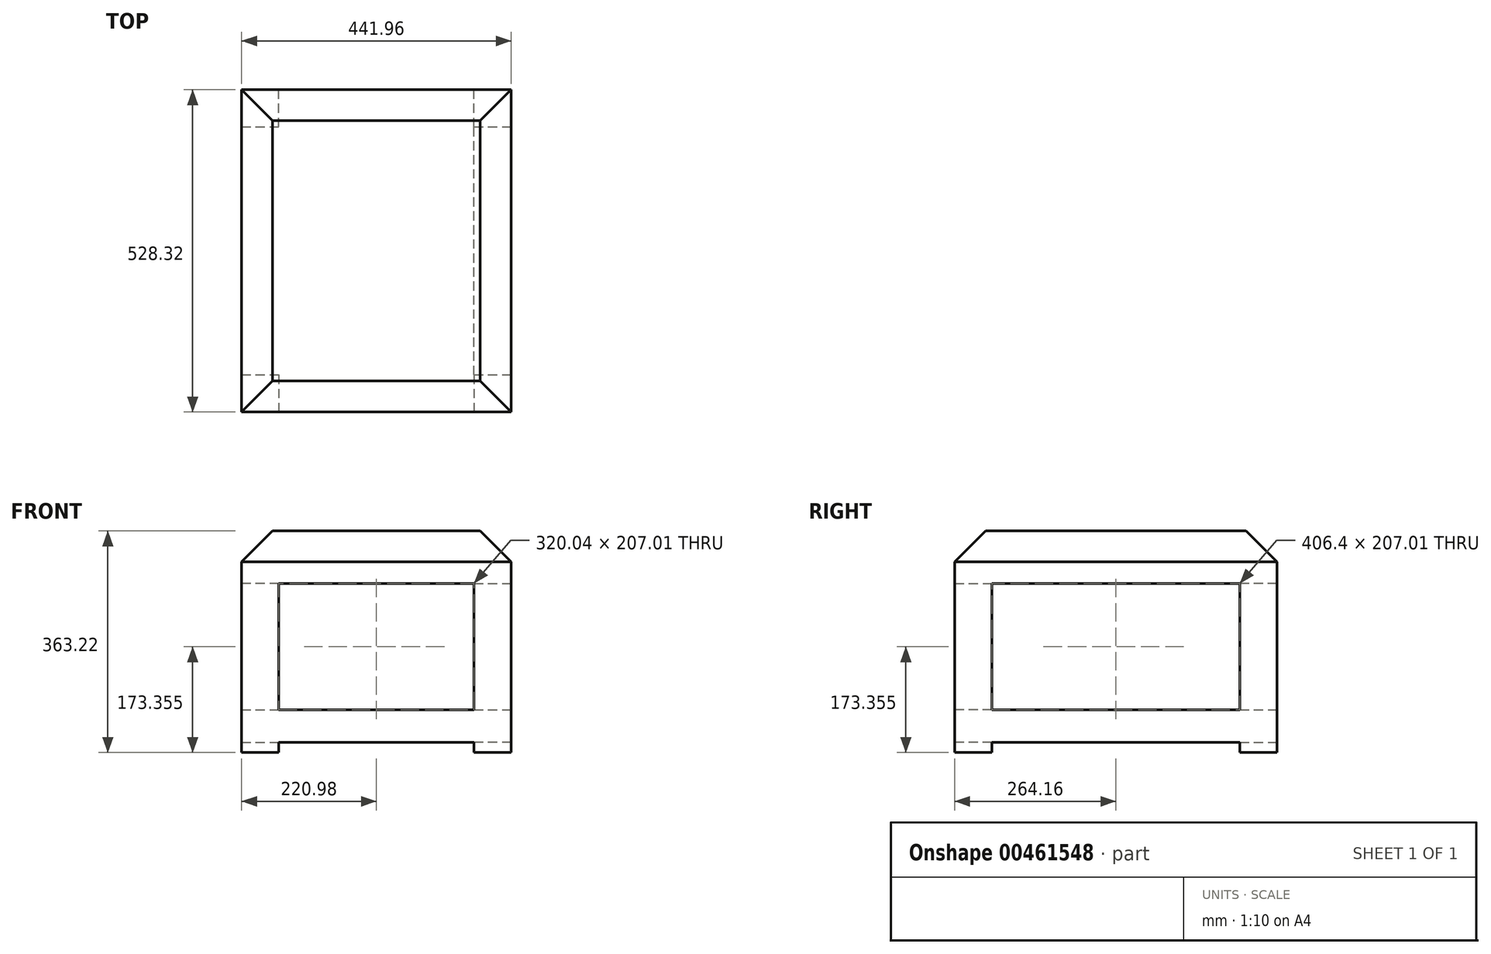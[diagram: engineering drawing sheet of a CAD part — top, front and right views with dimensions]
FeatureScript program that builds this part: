
annotation { "Feature Type Name" : "Feature", "Feature Type Description" : "" }
export const myFeature = defineFeature(function(context is Context, id is Id, definition is map)
    precondition{}
    {
        {
            var Q0;
            Q0=qCreatedBy(makeId("Top.planeOp"),FACE);
            var sketch = newSketch(context, id + "F0", { "sketchPlane" : qUnion([Q0])});
            skLineSegment(sketch, "E0", {"start": v(0, 0) * mm, "end": v(0, -264.16) * mm});
            skLineSegment(sketch, "E1", {"start": v(0, -264.16) * mm, "end": v(220.98, -264.16) * mm});
            skLineSegment(sketch, "E2", {"start": v(220.98, -264.16) * mm, "end": v(220.98, 0) * mm});
            skLineSegment(sketch, "E3", {"start": v(220.98, 0) * mm, "end": v(0, 0) * mm});
            skLineSegment(sketch, "E4", {"start": v(0, 0) * mm, "end": v(0, 264.16) * mm});
            skLineSegment(sketch, "E5", {"start": v(0, 264.16) * mm, "end": v(220.98, 264.16) * mm});
            skLineSegment(sketch, "E6", {"start": v(220.98, 264.16) * mm, "end": v(220.98, 0) * mm});
            skLineSegment(sketch, "E7", {"start": v(0, 0) * mm, "end": v(-220.98, 0) * mm});
            skLineSegment(sketch, "E8", {"start": v(-220.98, 0) * mm, "end": v(-220.98, -264.16) * mm});
            skLineSegment(sketch, "E9", {"start": v(-220.98, -264.16) * mm, "end": v(0, -264.16) * mm});
            skLineSegment(sketch, "E10", {"start": v(-220.98, 0) * mm, "end": v(-220.98, 264.16) * mm});
            skLineSegment(sketch, "E11", {"start": v(-220.98, 264.16) * mm, "end": v(0, 264.16) * mm});
            skSolve(sketch);
        }
        {
            var Q0;
            Q0 = qSketchRegion(id + "F0", true);
            extrude(context, id + "F1", {"entities" : qUnion([Q0]), "depth" : 53.34 * mm});
        }
        {
            var Q0;
            Q0=makeQuery(id+"F1.opExtrude","CAP_FACE",FACE,{"disambiguationData":[OSD([sQuery(id+"F0.wireOp",EDGE,"E1"),sQuery(id+"F0.wireOp",EDGE,"E2"),sQuery(id+"F0.wireOp",EDGE,"E5"),sQuery(id+"F0.wireOp",EDGE,"E6"),sQuery(id+"F0.wireOp",EDGE,"E8"),sQuery(id+"F0.wireOp",EDGE,"E9"),sQuery(id+"F0.wireOp",EDGE,"E10"),sQuery(id+"F0.wireOp",EDGE,"E11")])],"isStart":false});
            var sketch = newSketch(context, id + "F2", { "sketchPlane" : qUnion([Q0])});
            skLineSegment(sketch, "E12.0", {"start": v(0, 0) * mm, "end": v(0, -264.16) * mm});
            skLineSegment(sketch, "E13.0", {"start": v(0, 0) * mm, "end": v(-220.98, 0) * mm});
            skLineSegment(sketch, "E14.0", {"start": v(0, 0) * mm, "end": v(0, 264.16) * mm});
            skLineSegment(sketch, "E15.0", {"start": v(220.98, 0) * mm, "end": v(0, 0) * mm});
            skLineSegment(sketch, "E16", {"start": v(160.02, 264.16) * mm, "end": v(160.02, 203.2) * mm});
            skLineSegment(sketch, "E17", {"start": v(160.02, 203.2) * mm, "end": v(220.98, 203.2) * mm});
            skPoint(sketch, "E18.end.orphan", {"position": v(220.98, -11.85) * mm});
            skPoint(sketch, "E19.end.orphan", {"position": v(34.07, -264.16) * mm});
            skLineSegment(sketch, "E20.MirrorCS", {"start": v(160.02, -203.2) * mm, "end": v(220.98, -203.2) * mm});
            skLineSegment(sketch, "E21.MirrorCS", {"start": v(160.02, -264.16) * mm, "end": v(160.02, -203.2) * mm});
            skLineSegment(sketch, "E22.MirrorCS", {"start": v(-160.02, -264.16) * mm, "end": v(-160.02, -203.2) * mm});
            skLineSegment(sketch, "E23.MirrorCS", {"start": v(-160.02, -203.2) * mm, "end": v(-220.98, -203.2) * mm});
            skLineSegment(sketch, "E24.MirrorCS", {"start": v(-160.02, 203.2) * mm, "end": v(-220.98, 203.2) * mm});
            skLineSegment(sketch, "E25.MirrorCS", {"start": v(-160.02, 264.16) * mm, "end": v(-160.02, 203.2) * mm});
            skSolve(sketch);
        }
        {
            var Q0;
            Q0 = qSketchRegion(id + "F2", true);
            var Q1;
            {var subQ0=sQuery(id+"F2.wireOp",EDGE,"E22.MirrorCS");Q1=makeQuery(id+"F2.imprint","IMPRINT",FACE,{"disambiguationData":[TD([[makeQuery(id+"F2.imprint","IMPRINT",EDGE,{"derivedFrom":subQ0}),1.0]])]});}
            var Q2;
            {var subQ0=sQuery(id+"F2.wireOp",EDGE,"E24.MirrorCS");Q2=makeQuery(id+"F2.imprint","IMPRINT",FACE,{"disambiguationData":[TD([[makeQuery(id+"F2.imprint","IMPRINT",EDGE,{"derivedFrom":subQ0}),-1.0]])]});}
            var Q3;
            {var subQ0=sQuery(id+"F2.wireOp",EDGE,"E16");Q3=makeQuery(id+"F2.imprint","IMPRINT",FACE,{"disambiguationData":[TD([[makeQuery(id+"F2.imprint","IMPRINT",EDGE,{"derivedFrom":subQ0}),1.0]])]});}
            var Q4;
            {var subQ0=sQuery(id+"F2.wireOp",EDGE,"E20.MirrorCS");Q4=makeQuery(id+"F2.imprint","IMPRINT",FACE,{"disambiguationData":[TD([[makeQuery(id+"F2.imprint","IMPRINT",EDGE,{"derivedFrom":subQ0}),-1.0]])]});}
            extrude(context, id + "F3", {"entities" : qUnion([Q0, Q1, Q2, Q3, Q4]), "operationType" : NewBodyOperationType.ADD, "endBound" : BoundingType.SYMMETRIC, "depth" : 139.7 * mm});
        }
        {
            var Q0;
            Q0=makeQuery(id+"F3.opExtrude","CAP_FACE",FACE,{"disambiguationData":[OSD([sQuery(id+"F0.wireOp",EDGE,"E5"),sQuery(id+"F0.wireOp",EDGE,"E8"),sQuery(id+"F0.wireOp",EDGE,"E10"),sQuery(id+"F0.wireOp",EDGE,"E11"),sQuery(id+"F2.wireOp",EDGE,"E24.MirrorCS"),sQuery(id+"F2.wireOp",EDGE,"E25.MirrorCS")])],"isStart":false});
            var sketch = newSketch(context, id + "F4", { "sketchPlane" : qUnion([Q0])});
            skLineSegment(sketch, "E26.0", {"start": v(-160.02, -203.2) * mm, "end": v(-220.98, -203.2) * mm});
            skLineSegment(sketch, "E27.0", {"start": v(-160.02, -264.16) * mm, "end": v(-160.02, -203.2) * mm});
            skLineSegment(sketch, "E28.0", {"start": v(-220.98, -264.16) * mm, "end": v(-160.02, -264.16) * mm});
            skLineSegment(sketch, "E29.0", {"start": v(-220.98, -203.2) * mm, "end": v(-220.98, -264.16) * mm});
            skLineSegment(sketch, "E30.0", {"start": v(0, 0) * mm, "end": v(-220.98, 0) * mm});
            skLineSegment(sketch, "E31.0", {"start": v(0, 0) * mm, "end": v(0, 264.16) * mm});
            skLineSegment(sketch, "E32.0", {"start": v(220.98, 0) * mm, "end": v(0, 0) * mm});
            skLineSegment(sketch, "E33.0", {"start": v(0, 0) * mm, "end": v(0, -264.16) * mm});
            skLineSegment(sketch, "E34.MirrorCS", {"start": v(-160.02, 203.2) * mm, "end": v(-220.98, 203.2) * mm});
            skLineSegment(sketch, "E35.MirrorCS", {"start": v(-160.02, 264.16) * mm, "end": v(-160.02, 203.2) * mm});
            skLineSegment(sketch, "E36.MirrorCS", {"start": v(-220.98, 203.2) * mm, "end": v(-220.98, 264.16) * mm});
            skLineSegment(sketch, "E37.MirrorCS", {"start": v(-220.98, 264.16) * mm, "end": v(-160.02, 264.16) * mm});
            skLineSegment(sketch, "E38.MirrorCS", {"start": v(160.02, 264.16) * mm, "end": v(160.02, 203.2) * mm});
            skLineSegment(sketch, "E39.MirrorCS", {"start": v(220.98, 264.16) * mm, "end": v(160.02, 264.16) * mm});
            skLineSegment(sketch, "E40.MirrorCS", {"start": v(160.02, 203.2) * mm, "end": v(220.98, 203.2) * mm});
            skLineSegment(sketch, "E41.MirrorCS", {"start": v(220.98, 203.2) * mm, "end": v(220.98, 264.16) * mm});
            skLineSegment(sketch, "E42.MirrorCS", {"start": v(160.02, -203.2) * mm, "end": v(220.98, -203.2) * mm});
            skLineSegment(sketch, "E43.MirrorCS", {"start": v(160.02, -264.16) * mm, "end": v(160.02, -203.2) * mm});
            skLineSegment(sketch, "E44.MirrorCS", {"start": v(220.98, -264.16) * mm, "end": v(160.02, -264.16) * mm});
            skLineSegment(sketch, "E45.MirrorCS", {"start": v(220.98, -203.2) * mm, "end": v(220.98, -264.16) * mm});
            skSolve(sketch);
        }
        {
            var Q0;
            Q0 = qSketchRegion(id + "F4", true);
            extrude(context, id + "F5", {"entities" : qUnion([Q0]), "operationType" : NewBodyOperationType.ADD, "depth" : 137.16 * mm});
        }
        {
            var Q0;
            Q0=makeQuery(id+"F5.opExtrude","CAP_FACE",FACE,{"disambiguationData":[OSD([sQuery(id+"F4.wireOp",EDGE,"E34.MirrorCS"),sQuery(id+"F4.wireOp",EDGE,"E35.MirrorCS"),sQuery(id+"F4.wireOp",EDGE,"E36.MirrorCS"),sQuery(id+"F4.wireOp",EDGE,"E37.MirrorCS")])],"isStart":false});
            var sketch = newSketch(context, id + "F6", { "sketchPlane" : qUnion([Q0])});
            skLineSegment(sketch, "E46.0", {"start": v(-160.02, 203.2) * mm, "end": v(-220.98, 203.2) * mm});
            skLineSegment(sketch, "E47.0", {"start": v(-160.02, 264.16) * mm, "end": v(-160.02, 203.2) * mm});
            skLineSegment(sketch, "E48.0", {"start": v(-220.98, 264.16) * mm, "end": v(-160.02, 264.16) * mm});
            skLineSegment(sketch, "E49.0", {"start": v(-220.98, 264.16) * mm, "end": v(-220.98, 203.2) * mm});
            skLineSegment(sketch, "E50.0", {"start": v(-160.02, -203.2) * mm, "end": v(-220.98, -203.2) * mm});
            skLineSegment(sketch, "E51.0", {"start": v(-160.02, -264.16) * mm, "end": v(-160.02, -203.2) * mm});
            skLineSegment(sketch, "E52.0", {"start": v(-220.98, -264.16) * mm, "end": v(-160.02, -264.16) * mm});
            skLineSegment(sketch, "E53.0", {"start": v(-220.98, -203.2) * mm, "end": v(-220.98, -264.16) * mm});
            skLineSegment(sketch, "E54.0", {"start": v(160.02, -264.16) * mm, "end": v(160.02, -203.2) * mm});
            skLineSegment(sketch, "E55.0", {"start": v(160.02, -203.2) * mm, "end": v(220.98, -203.2) * mm});
            skLineSegment(sketch, "E56.0", {"start": v(220.98, -264.16) * mm, "end": v(160.02, -264.16) * mm});
            skLineSegment(sketch, "E57.0", {"start": v(220.98, -203.2) * mm, "end": v(220.98, -264.16) * mm});
            skLineSegment(sketch, "E58.0", {"start": v(160.02, 203.2) * mm, "end": v(220.98, 203.2) * mm});
            skLineSegment(sketch, "E59.0", {"start": v(160.02, 264.16) * mm, "end": v(160.02, 203.2) * mm});
            skLineSegment(sketch, "E60.0", {"start": v(220.98, 264.16) * mm, "end": v(160.02, 264.16) * mm});
            skLineSegment(sketch, "E61.0", {"start": v(220.98, 203.2) * mm, "end": v(220.98, 264.16) * mm});
            skLineSegment(sketch, "E62", {"start": v(-220.98, 264.16) * mm, "end": v(-220.98, -264.16) * mm});
            skLineSegment(sketch, "E63", {"start": v(-220.98, -264.16) * mm, "end": v(220.98, -264.16) * mm});
            skLineSegment(sketch, "E64", {"start": v(220.98, -264.16) * mm, "end": v(220.98, 264.16) * mm});
            skLineSegment(sketch, "E65", {"start": v(220.98, 264.16) * mm, "end": v(-220.98, 264.16) * mm});
            skSolve(sketch);
        }
        {
            var Q0;
            Q0 = qSketchRegion(id + "F6", true);
            extrude(context, id + "F7", {"entities" : qUnion([Q0]), "operationType" : NewBodyOperationType.ADD, "depth" : 7.62 * mm});
        }
        {
            var Q0;
            Q0=makeQuery(id+"F7.opExtrude","CAP_FACE",FACE,{"disambiguationData":[OSD([sQuery(id+"F6.wireOp",EDGE,"E62"),sQuery(id+"F6.wireOp",EDGE,"E63"),sQuery(id+"F6.wireOp",EDGE,"E64"),sQuery(id+"F6.wireOp",EDGE,"E65")])],"isStart":false});
            var sketch = newSketch(context, id + "F8", { "sketchPlane" : qUnion([Q0])});
            skLineSegment(sketch, "E66.0", {"start": v(-220.98, 264.16) * mm, "end": v(220.98, 264.16) * mm});
            skLineSegment(sketch, "E67.0", {"start": v(220.98, -264.16) * mm, "end": v(220.98, 264.16) * mm});
            skLineSegment(sketch, "E68.0", {"start": v(-220.98, -264.16) * mm, "end": v(220.98, -264.16) * mm});
            skLineSegment(sketch, "E69.0", {"start": v(-220.98, 264.16) * mm, "end": v(-220.98, -264.16) * mm});
            skSolve(sketch);
        }
        {
            var Q0;
            Q0 = qSketchRegion(id + "F8", true);
            extrude(context, id + "F9", {"entities" : qUnion([Q0]), "operationType" : NewBodyOperationType.ADD, "depth" : 78.74 * mm});
        }
        {
            var Q0;
            Q0=makeQuery(id+"F9.opExtrude","CAP_EDGE",EDGE,{"disambiguationData":[OSD([sQuery(id+"F8.wireOp",EDGE,"E69.0")])],"isStart":false});
            var Q1;
            Q1=makeQuery(id+"F9.opExtrude","CAP_EDGE",EDGE,{"disambiguationData":[OSD([sQuery(id+"F8.wireOp",EDGE,"E66.0")])],"isStart":false});
            var Q2;
            Q2=makeQuery(id+"F9.opExtrude","CAP_EDGE",EDGE,{"disambiguationData":[OSD([sQuery(id+"F8.wireOp",EDGE,"E67.0")])],"isStart":false});
            var Q3;
            Q3=makeQuery(id+"F9.opExtrude","CAP_EDGE",EDGE,{"disambiguationData":[OSD([sQuery(id+"F8.wireOp",EDGE,"E68.0")])],"isStart":false});
            chamfer(context, id + "F10", {"entities" : qUnion([Q0, Q1, Q2, Q3]), "width" : 50.8 * mm, "tangentPropagation" : true});
        }
        {
            var Q0;
            {var subQ0=sQuery(id+"F0.wireOp",EDGE,"E6");var subQ1=sQuery(id+"F0.wireOp",EDGE,"E2");var subQ2=makeQuery(id+"F1.opExtrude","CAP_EDGE",EDGE,{"disambiguationData":[OSD([subQ1,subQ0])],"isStart":false});Q0=makeQuery(id+"F9.boolean.opBoolean","MERGE",FACE,{"derivedFrom":[makeQuery(id+"F7.boolean.opBoolean","MERGE",FACE,{"derivedFrom":[makeQuery(id+"F5.boolean.opBoolean","MERGE",FACE,{"derivedFrom":[makeQuery(id+"F3.boolean.opBoolean","MERGE",FACE,{"derivedFrom":[makeQuery(id+"F1.opExtrude","SWEPT_FACE",FACE,{"disambiguationData":[OSD([subQ1,subQ0])]}),makeQuery(id+"F3.opExtrude","SWEPT_FACE",FACE,{"disambiguationData":[OSD([subQ1,subQ0]),TDD([makeQuery(id+"F2.imprint","IMPRINT",EDGE,{"disambiguationData":[TD([[makeQuery(id+"F2.imprint","INTERSECT",VERTEX,{"derivedFrom":[subQ2,sQuery(id+"F2.wireOp",EDGE,"E20.MirrorCS")]}),1.0]])],"derivedFrom":subQ2})])]}),makeQuery(id+"F3.opExtrude","SWEPT_FACE",FACE,{"disambiguationData":[OSD([subQ1,subQ0]),TDD([makeQuery(id+"F2.imprint","IMPRINT",EDGE,{"disambiguationData":[TD([[makeQuery(id+"F2.imprint","INTERSECT",VERTEX,{"derivedFrom":[subQ2,sQuery(id+"F2.wireOp",EDGE,"E17")]}),-1.0]])],"derivedFrom":subQ2})])]})]}),makeQuery(id+"F5.opExtrude","SWEPT_FACE",FACE,{"disambiguationData":[OSD([sQuery(id+"F4.wireOp",EDGE,"E41.MirrorCS")])]}),makeQuery(id+"F5.opExtrude","SWEPT_FACE",FACE,{"disambiguationData":[OSD([sQuery(id+"F4.wireOp",EDGE,"E45.MirrorCS")])]})]}),makeQuery(id+"F7.opExtrude","SWEPT_FACE",FACE,{"disambiguationData":[OSD([sQuery(id+"F6.wireOp",EDGE,"E64")])]})]}),makeQuery(id+"F9.opExtrude","SWEPT_FACE",FACE,{"disambiguationData":[OSD([sQuery(id+"F8.wireOp",EDGE,"E67.0")])]})]});}
            var sketch = newSketch(context, id + "F11", { "sketchPlane" : qUnion([Q0])});
            skLineSegment(sketch, "E70.0", {"start": v(-203.2, 53.34) * mm, "end": v(203.2, 53.34) * mm});
            skLineSegment(sketch, "E71.0", {"start": v(-203.2, 260.35) * mm, "end": v(-203.2, 53.34) * mm});
            skLineSegment(sketch, "E72.0", {"start": v(-203.2, 260.35) * mm, "end": v(203.2, 260.35) * mm});
            skLineSegment(sketch, "E73.0", {"start": v(203.2, 260.35) * mm, "end": v(203.2, 53.34) * mm});
            skSolve(sketch);
        }
        {
            var Q0;
            Q0 = qSketchRegion(id + "F11", true);
            extrude(context, id + "F12", {"entities" : qUnion([Q0]), "oppositeDirection" : true, "depth" : 60.96 * mm});
        }
    });
